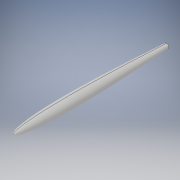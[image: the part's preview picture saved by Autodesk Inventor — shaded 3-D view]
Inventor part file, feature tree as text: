
AUTODESK INVENTOR PART (.ipt)
format: ipt  version: 2019.3 (Build 233278000, 278)  size: 176,128 bytes
history: native  units: mm
features: sketch x3, revolve x2, plane x2, other x2, extrude x1
ambient origin geometry x8: Origin, YZ Plane, XZ Plane, XY Plane, X Axis, Y Axis, Z Axis, Center Point
bodies: Body1 (feature_tree)
feature tree (10):
  revolve  "Revolution1"  Angle=90.0deg
  revolve  "Revolution2"  [1 undecoded]
  plane  "Work Plane3"
  extrude  "Extrusion6"  Depth=9000.0mm
  plane  "Work Plane4"
  sketch  "Sketch1"  dims[d0=0.0mm d1=10.0mm d13=90.0deg]
  other  "2D Equation Curve1"
  sketch  "Sketch8"  dims[d41=0.0mm d42=10.0mm d43=20.0mm d45=687.5mm]
  other  "2D Equation Curve6"
  sketch  "Sketch9"  dims[d46=10.0mm d48=10.0mm d50=7012.5mm d52=90.0deg d53=9000.0mm d54=660.0mm d55=2500.0mm d56=0.0mm d85=2750.0mm]
note: 1 required parameter value undecoded (feature->parameter linkage not recoverable at this tier; creation-order binding heuristic only, values carry confidence <= 0.55)
